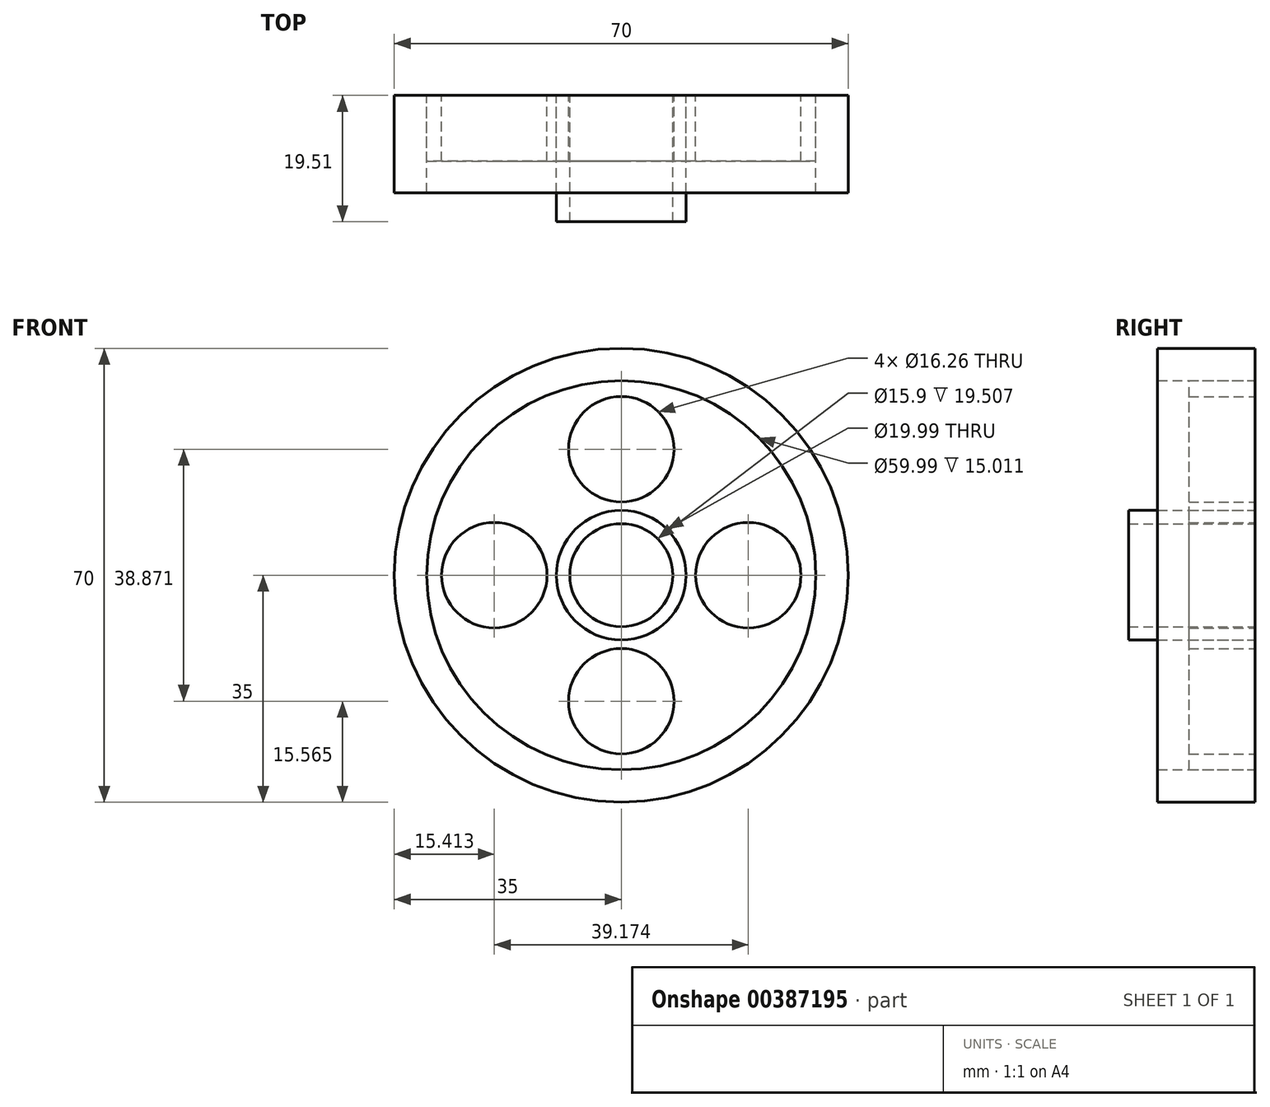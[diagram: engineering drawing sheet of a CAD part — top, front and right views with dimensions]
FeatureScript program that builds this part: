
annotation { "Feature Type Name" : "Feature", "Feature Type Description" : "" }
export const myFeature = defineFeature(function(context is Context, id is Id, definition is map)
    precondition{}
    {
        {
            var Q0;
            Q0=qCreatedBy(makeId("Front.planeOp"),FACE);
            var sketch = newSketch(context, id + "F0", { "sketchPlane" : qUnion([Q0])});
            skCircle(sketch, "E0", {"center": v(0, 0) * mm, "radius": 35 * mm});
            skCircle(sketch, "E1", {"center": v(0, 0) * mm, "radius": 30 * mm});
            skCircle(sketch, "E2", {"center": v(0, 0) * mm, "radius": 10 * mm});
            skCircle(sketch, "E3", {"center": v(0, 0) * mm, "radius": 7.95 * mm});
            skCircle(sketch, "E4", {"center": v(0, 19.44) * mm, "radius": 8.13 * mm});
            skCircle(sketch, "E5.MirrorC", {"center": v(0, -19.44) * mm, "radius": 8.13 * mm});
            skCircle(sketch, "E6", {"center": v(19.59, 0) * mm, "radius": 8.13 * mm});
            skCircle(sketch, "E7.MirrorC", {"center": v(-19.59, 0) * mm, "radius": 8.13 * mm});
            skSolve(sketch);
        }
        {
            var Q0;
            Q0=makeQuery(id+"F0.imprint","IMPRINT",FACE,{"disambiguationData":[TD([[makeQuery(id+"F0.imprint","IMPRINT",EDGE,{"derivedFrom":sQuery(id+"F0.wireOp",EDGE,"E0")}),1.0]])]});
            extrude(context, id + "F1", {"entities" : qUnion([Q0]), "depth" : 15 * mm});
        }
        {
            var Q0;
            Q0=makeQuery(id+"F0.imprint","IMPRINT",FACE,{"disambiguationData":[TD([[makeQuery(id+"F0.imprint","IMPRINT",EDGE,{"derivedFrom":sQuery(id+"F0.wireOp",EDGE,"E2")}),1.0]])]});
            extrude(context, id + "F2", {"entities" : qUnion([Q0]), "depth" : 19.5 * mm});
        }
        {
            var Q0;
            Q0=makeQuery(id+"F0.imprint","IMPRINT",FACE,{"disambiguationData":[TD([[makeQuery(id+"F0.imprint","IMPRINT",EDGE,{"derivedFrom":sQuery(id+"F0.wireOp",EDGE,"E1")}),1.0]])]});
            extrude(context, id + "F3", {"entities" : qUnion([Q0]), "depth" : 10.16 * mm});
        }
    });
